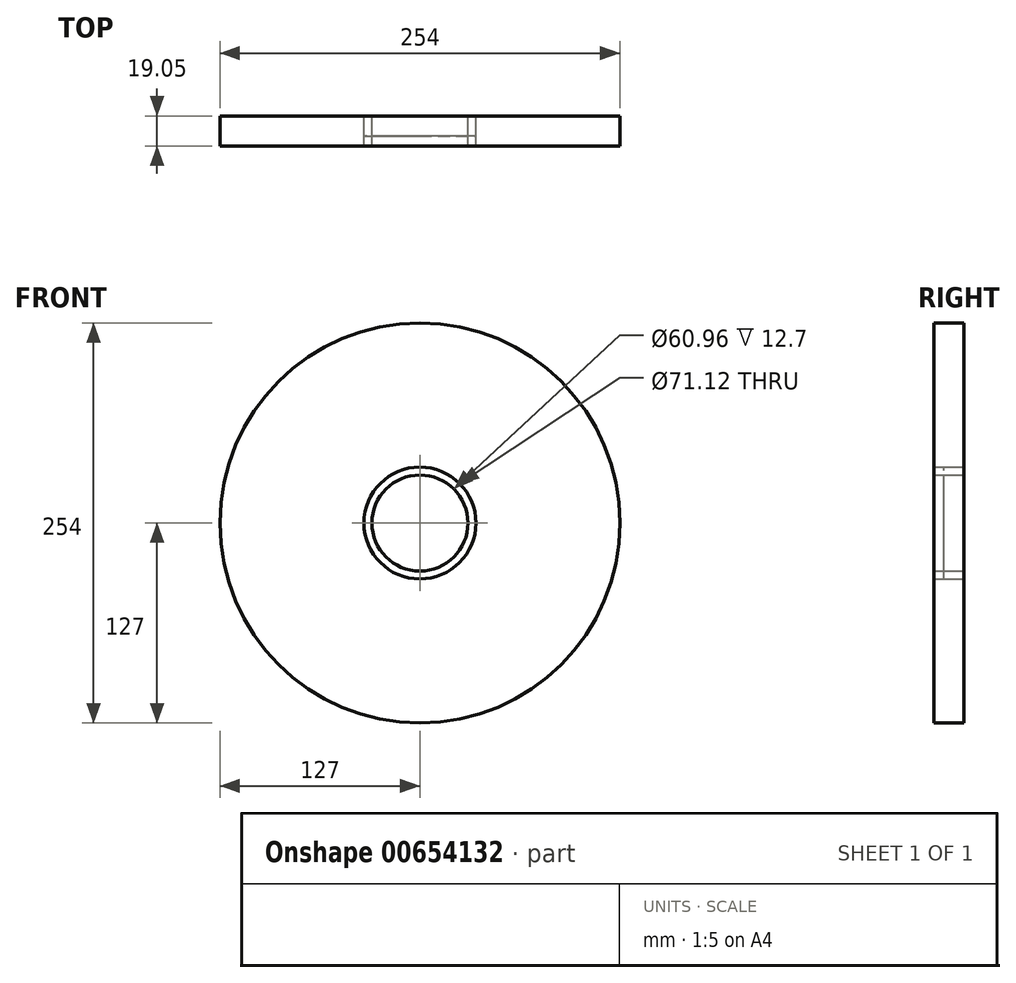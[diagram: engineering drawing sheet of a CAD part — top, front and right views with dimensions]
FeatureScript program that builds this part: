
annotation { "Feature Type Name" : "Feature", "Feature Type Description" : "" }
export const myFeature = defineFeature(function(context is Context, id is Id, definition is map)
    precondition{}
    {
        {
            var Q0;
            Q0=qCreatedBy(makeId("Front.planeOp"),FACE);
            var sketch = newSketch(context, id + "F0", { "sketchPlane" : qUnion([Q0])});
            skCircle(sketch, "E0", {"center": v(0, 0) * mm, "radius": 127 * mm});
            skCircle(sketch, "E1", {"center": v(0, 0) * mm, "radius": 35.56 * mm});
            skCircle(sketch, "E2", {"center": v(0, 0) * mm, "radius": 30.48 * mm});
            skSolve(sketch);
        }
        {
            var Q0;
            Q0=makeQuery(id+"F0.imprint","IMPRINT",FACE,{"disambiguationData":[TD([[makeQuery(id+"F0.imprint","IMPRINT",EDGE,{"derivedFrom":sQuery(id+"F0.wireOp",EDGE,"E0")}),1.0]])]});
            var Q1;
            Q1=makeQuery(id+"F0.imprint","IMPRINT",FACE,{"disambiguationData":[TD([[makeQuery(id+"F0.imprint","IMPRINT",EDGE,{"derivedFrom":sQuery(id+"F0.wireOp",EDGE,"E2")}),1.0]])]});
            extrude(context, id + "F1", {"entities" : qUnion([Q0, Q1]), "depth" : 19.05 * mm, "offsetDistance" : 25.4 * mm});
        }
        {
            var Q0;
            Q0=makeQuery(id+"F0.imprint","IMPRINT",FACE,{"disambiguationData":[TD([[makeQuery(id+"F0.imprint","IMPRINT",EDGE,{"derivedFrom":sQuery(id+"F0.wireOp",EDGE,"E1")}),1.0]])]});
            extrude(context, id + "F2", {"entities" : qUnion([Q0]), "depth" : 12.7 * mm, "offsetDistance" : 25.4 * mm});
        }
    });
